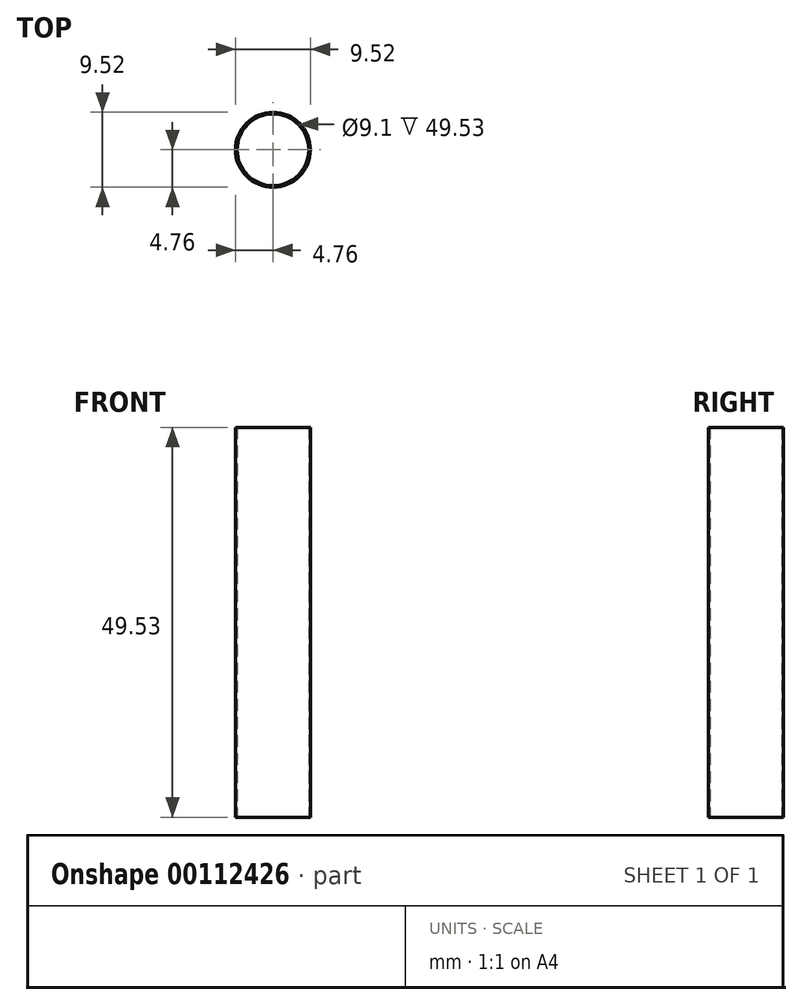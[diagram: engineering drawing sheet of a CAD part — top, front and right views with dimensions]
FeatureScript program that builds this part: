
annotation { "Feature Type Name" : "Feature", "Feature Type Description" : "" }
export const myFeature = defineFeature(function(context is Context, id is Id, definition is map)
    precondition{}
    {
        {
            var Q0;
            Q0=qCreatedBy(makeId("Top.planeOp"),FACE);
            var sketch = newSketch(context, id + "F0", { "sketchPlane" : qUnion([Q0])});
            skCircle(sketch, "E0", {"center": v(0, 0) * mm, "radius": 4.76 * mm});
            skCircle(sketch, "E1", {"center": v(0, 0) * mm, "radius": 4.55 * mm});
            skSolve(sketch);
        }
        {
            var Q0;
            Q0 = qSketchRegion(id + "F0", true);
            extrude(context, id + "F1", {"entities" : qUnion([Q0]), "depth" : 49.53 * mm, "offsetDistance" : 25 * mm});
        }
    });
